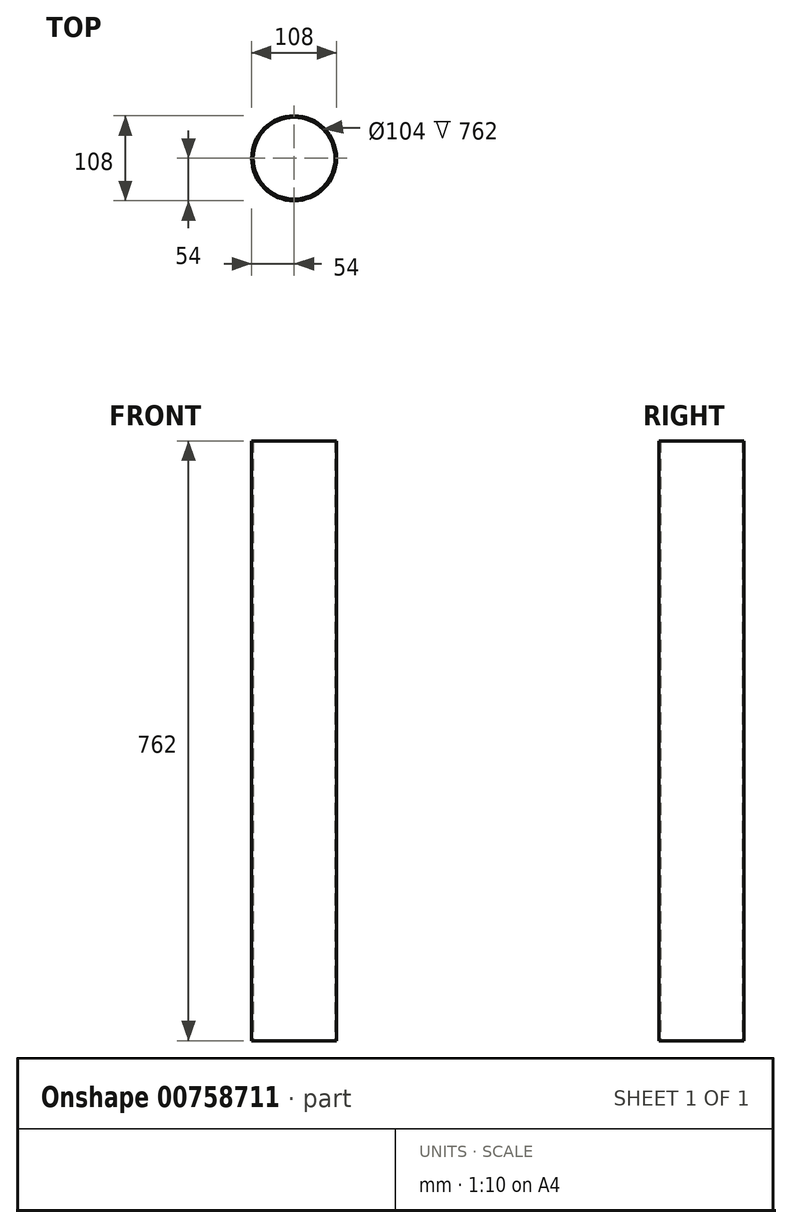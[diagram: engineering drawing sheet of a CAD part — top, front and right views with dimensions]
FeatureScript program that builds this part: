
annotation { "Feature Type Name" : "Feature", "Feature Type Description" : "" }
export const myFeature = defineFeature(function(context is Context, id is Id, definition is map)
    precondition{}
    {
        {
            var Q0;
            Q0=qCreatedBy(makeId("Top.planeOp"),FACE);
            var sketch = newSketch(context, id + "F0", { "sketchPlane" : qUnion([Q0])});
            skCircle(sketch, "E0", {"center": v(0, 0) * mm, "radius": 54 * mm});
            skCircle(sketch, "E1", {"center": v(0, 0) * mm, "radius": 52 * mm});
            skSolve(sketch);
        }
        {
            var Q0;
            Q0=makeQuery(id+"F0.imprint","IMPRINT",FACE,{"disambiguationData":[TD([[makeQuery(id+"F0.imprint","IMPRINT",EDGE,{"derivedFrom":sQuery(id+"F0.wireOp",EDGE,"E0")}),1.0]])]});
            extrude(context, id + "F1", {"entities" : qUnion([Q0]), "depth" : 762 * mm, "offsetDistance" : 25 * mm});
        }
    });
